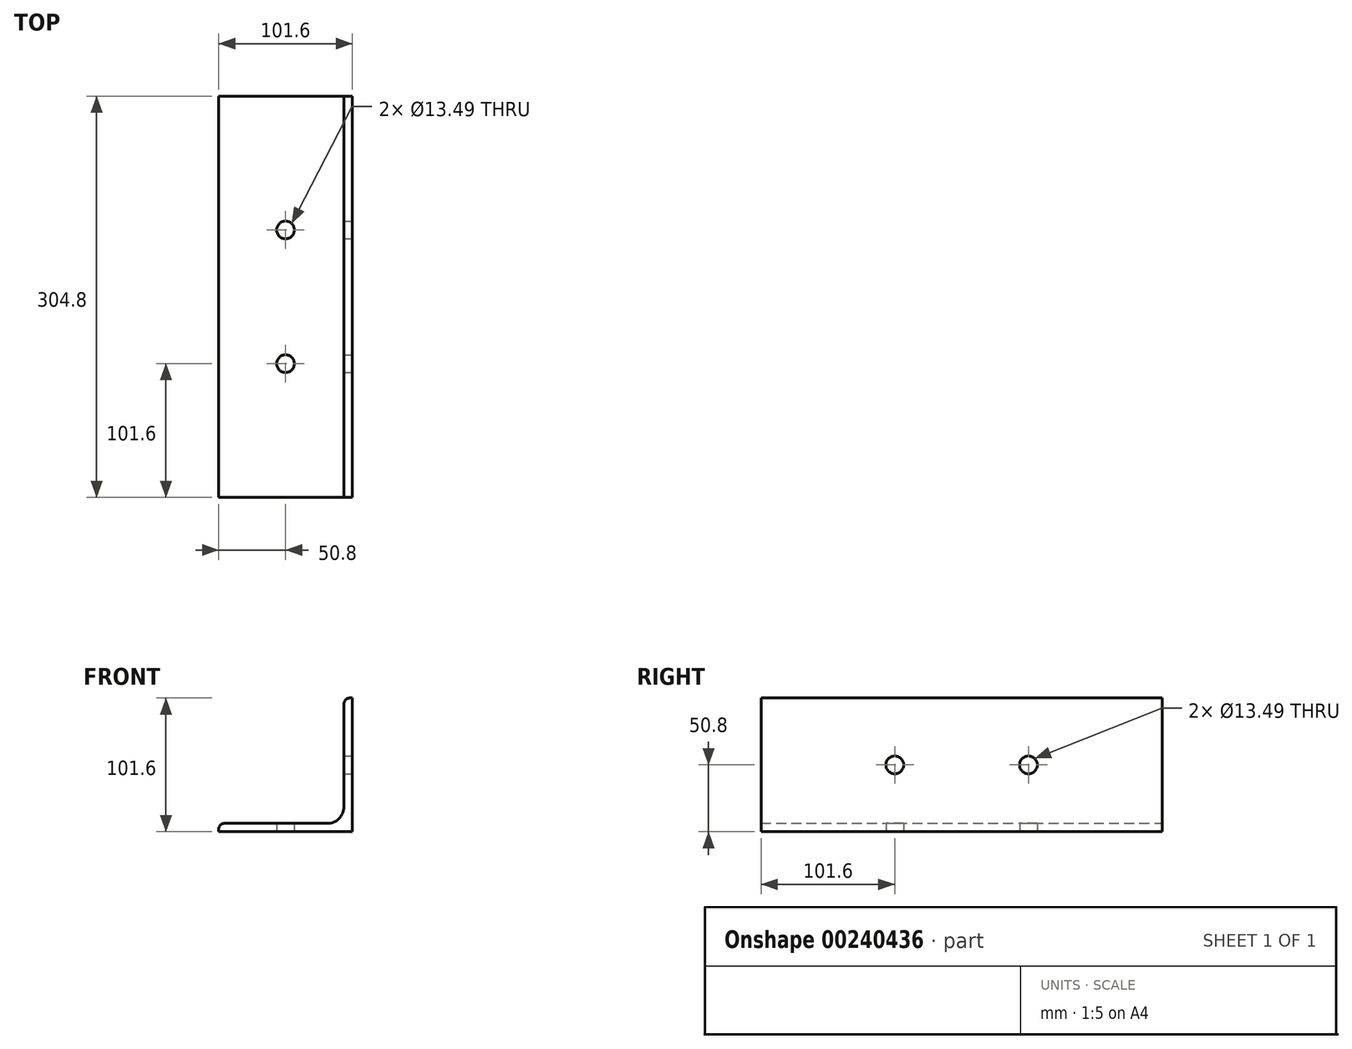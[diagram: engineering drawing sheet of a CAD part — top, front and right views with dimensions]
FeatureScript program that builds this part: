
annotation { "Feature Type Name" : "Feature", "Feature Type Description" : "" }
export const myFeature = defineFeature(function(context is Context, id is Id, definition is map)
    precondition{}
    {
        {
            var Q0;
            Q0=qCreatedBy(makeId("Front.planeOp"),FACE);
            var sketch = newSketch(context, id + "F0", { "sketchPlane" : qUnion([Q0])});
            skLineSegment(sketch, "E0", {"start": v(-101.6, 0) * mm, "end": v(0, 0) * mm});
            skLineSegment(sketch, "E1", {"start": v(0, 0) * mm, "end": v(0, 101.6) * mm});
            skLineSegment(sketch, "E2", {"start": v(0, 101.6) * mm, "end": v(-1.9, 101.6) * mm});
            skLineSegment(sketch, "E3", {"start": v(-6.35, 97.16) * mm, "end": v(-6.35, 19.05) * mm});
            skLineSegment(sketch, "E4", {"start": v(-19.05, 6.35) * mm, "end": v(-97.16, 6.35) * mm});
            skLineSegment(sketch, "E5", {"start": v(-101.6, 1.9) * mm, "end": v(-101.6, 0) * mm});
            skPoint(sketch, "E6.visualSharp", {"position": v(-101.6, 6.35) * mm});
            skArc(sketch, "E6.filletArc", {"start": v(-97.16, 6.35) * mm, "mid": v(-100.3, 5.05) * mm, "end": v(-101.6, 1.9) * mm});
            skPoint(sketch, "E7.visualSharp", {"position": v(-6.35, 101.6) * mm});
            skArc(sketch, "E7.filletArc", {"start": v(-1.9, 101.6) * mm, "mid": v(-5.05, 100.3) * mm, "end": v(-6.35, 97.16) * mm});
            skPoint(sketch, "E8.visualSharp", {"position": v(-6.35, 6.35) * mm});
            skArc(sketch, "E8.filletArc", {"start": v(-19.05, 6.35) * mm, "mid": v(-10.07, 10.07) * mm, "end": v(-6.35, 19.05) * mm});
            skSolve(sketch);
        }
        {
            var Q0;
            Q0=makeQuery(id+"F0.imprint","IMPRINT",FACE,{"disambiguationData":[TD([[makeQuery(id+"F0.imprint","IMPRINT",EDGE,{"derivedFrom":sQuery(id+"F0.wireOp",EDGE,"E0")}),1.0]])]});
            extrude(context, id + "F1", {"entities" : qUnion([Q0]), "endBound" : BoundingType.SYMMETRIC, "depth" : 304.8 * mm});
        }
        {
            var Q0;
            Q0=makeQuery(id+"F1.opExtrude","SWEPT_FACE",FACE,{"disambiguationData":[OSD([sQuery(id+"F0.wireOp",EDGE,"E0")])]});
            var sketch = newSketch(context, id + "F2", { "sketchPlane" : qUnion([Q0])});
            skLineSegment(sketch, "E9", {"start": v(-50.8, 152.4) * mm, "end": v(-50.8, 50.8) * mm});
            skLineSegment(sketch, "E10", {"start": v(-50.8, 50.8) * mm, "end": v(-50.8, -50.8) * mm});
            skLineSegment(sketch, "E11", {"start": v(-50.8, -50.8) * mm, "end": v(-50.8, -152.4) * mm});
            skSolve(sketch);
        }
        {
            var Q0;
            Q0=makeQuery(id+"F1.opExtrude","SWEPT_FACE",FACE,{"disambiguationData":[OSD([sQuery(id+"F0.wireOp",EDGE,"E1")])]});
            var sketch = newSketch(context, id + "F3", { "sketchPlane" : qUnion([Q0])});
            skLineSegment(sketch, "E12", {"start": v(-152.4, 50.8) * mm, "end": v(-50.8, 50.8) * mm});
            skLineSegment(sketch, "E13", {"start": v(-50.8, 50.8) * mm, "end": v(50.8, 50.8) * mm});
            skLineSegment(sketch, "E14", {"start": v(50.8, 50.8) * mm, "end": v(152.4, 50.8) * mm});
            skSolve(sketch);
        }
        {
            var Q0;
            Q0=sQuery(id+"F3.wireOp",VERTEX,"E13.start");
            var Q1;
            Q1=sQuery(id+"F3.wireOp",VERTEX,"E14.start");
            var Q2;
            Q2=sQuery(id+"F2.wireOp",VERTEX,"E10.start");
            var Q3;
            Q3=sQuery(id+"F2.wireOp",VERTEX,"E11.start");
            var Q4;
            Q4=makeQuery(id+"F1.opExtrude","SWEPT_BODY",BODY,{"disambiguationData":[OSD([sQuery(id+"F0.wireOp",EDGE,"E0"),sQuery(id+"F0.wireOp",EDGE,"E1"),sQuery(id+"F0.wireOp",EDGE,"E2"),sQuery(id+"F0.wireOp",EDGE,"E3"),sQuery(id+"F0.wireOp",EDGE,"E4"),sQuery(id+"F0.wireOp",EDGE,"E5"),sQuery(id+"F0.wireOp",EDGE,"E6.filletArc"),sQuery(id+"F0.wireOp",EDGE,"E7.filletArc"),sQuery(id+"F0.wireOp",EDGE,"E8.filletArc")])]});
            hole(context, id + "F4", {"style" : HoleStyle.SIMPLE, "endStyle" : HoleEndStyle.THROUGH, "standardTappedOrClearance" : lookupTablePath({ "standard" : "ANSI", "fit" : "Normal (ASME)", "size" : "1/2", "type" : "Clearance" }), "standardBlindInLast" : lookupTablePath({ "fit" : "Free", "standard" : "ANSI", "size" : "1/2", "type" : "Clearance" }), "holeDiameter" : 13.5 * mm, "tappedDepth" : 12.7 * mm, "tapClearance" : 3, "locations" : qUnion([Q0, Q1, Q2, Q3]), "scope" : qUnion([Q4])});
        }
    });
